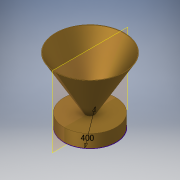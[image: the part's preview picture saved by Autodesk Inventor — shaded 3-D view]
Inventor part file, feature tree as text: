
AUTODESK INVENTOR PART (.ipt)
format: ipt  version: 2019.1 (Build 231200000, 200)  size: 130,560 bytes
history: native  units: mm
features: sketch x2, other x1, extrude x1, revolve x1, projected_geometry x1
ambient origin geometry x8: Origin, YZ Plane, XZ Plane, XY Plane, X Axis, Y Axis, Z Axis, Center Point
bodies: Body1 (feature_tree)
feature tree (6):
  other  "ソリッド1"
  extrude  "押し出し1"  Depth=400.0mm
  revolve  "回転1"
  sketch  "スケッチ1"
  sketch  "スケッチ2"
  projected_geometry  "投影ループ1"
